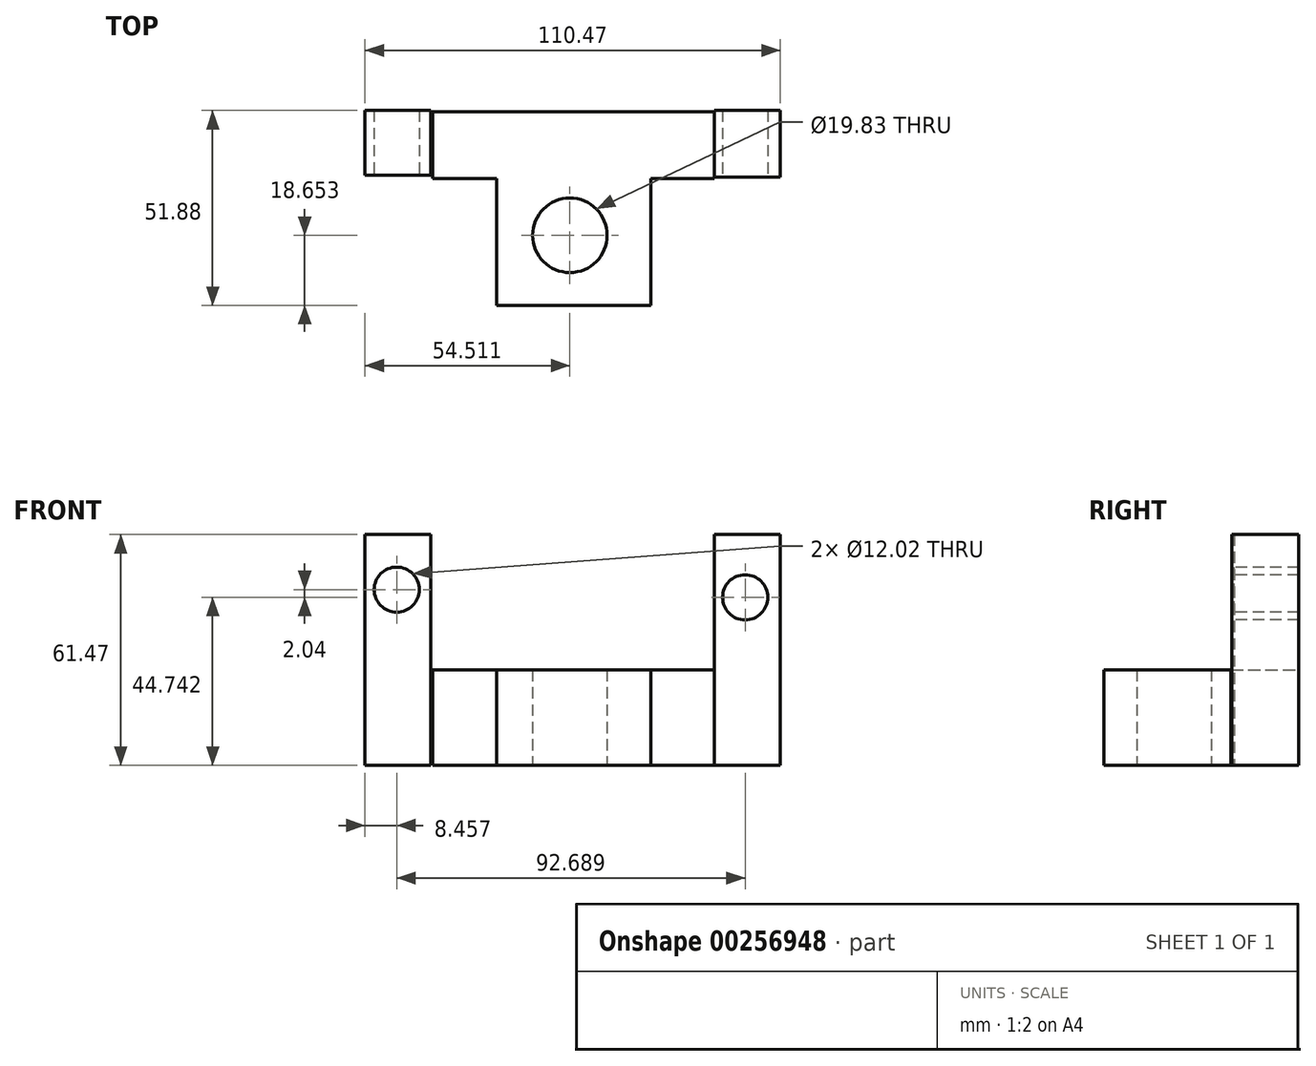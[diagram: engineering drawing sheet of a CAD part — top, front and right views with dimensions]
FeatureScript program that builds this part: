
annotation { "Feature Type Name" : "Feature", "Feature Type Description" : "" }
export const myFeature = defineFeature(function(context is Context, id is Id, definition is map)
    precondition{}
    {
        {
            var Q0;
            Q0=qCreatedBy(makeId("Top.planeOp"),FACE);
            var sketch = newSketch(context, id + "F0", { "sketchPlane" : qUnion([Q0])});
            skLineSegment(sketch, "E0", {"start": v(-25.36, 18.8) * mm, "end": v(-25.36, -15.01) * mm});
            skLineSegment(sketch, "E1", {"start": v(-25.36, -15.01) * mm, "end": v(15.74, -15.01) * mm});
            skLineSegment(sketch, "E2", {"start": v(15.74, -15.01) * mm, "end": v(15.74, 18.8) * mm});
            skLineSegment(sketch, "E3", {"start": v(15.74, 18.8) * mm, "end": v(32.65, 18.8) * mm});
            skLineSegment(sketch, "E4", {"start": v(32.65, 18.8) * mm, "end": v(32.65, 36.58) * mm});
            skLineSegment(sketch, "E5", {"start": v(-25.36, 18.8) * mm, "end": v(-42.26, 18.8) * mm});
            skLineSegment(sketch, "E6", {"start": v(-42.26, 18.8) * mm, "end": v(-42.26, 36.58) * mm});
            skLineSegment(sketch, "E7", {"start": v(-42.26, 36.58) * mm, "end": v(32.65, 36.58) * mm});
            skSolve(sketch);
        }
        {
            var Q0;
            Q0 = qSketchRegion(id + "F0", true);
            extrude(context, id + "F1", {"entities" : qUnion([Q0]), "depth" : 25.4 * mm});
        }
        {
            var Q0;
            Q0=qCreatedBy(makeId("Top.planeOp"),FACE);
            var sketch = newSketch(context, id + "F2", { "sketchPlane" : qUnion([Q0])});
            skLineSegment(sketch, "E8", {"start": v(32.65, 36.87) * mm, "end": v(32.65, 19.1) * mm});
            skLineSegment(sketch, "E9", {"start": v(32.65, 19.1) * mm, "end": v(50.13, 19.1) * mm});
            skLineSegment(sketch, "E10", {"start": v(50.13, 19.1) * mm, "end": v(50.13, 36.87) * mm});
            skLineSegment(sketch, "E11", {"start": v(50.13, 36.87) * mm, "end": v(32.65, 36.87) * mm});
            skLineSegment(sketch, "E12", {"start": v(-42.85, 36.87) * mm, "end": v(-60.34, 36.87) * mm});
            skLineSegment(sketch, "E13", {"start": v(-42.85, 36.87) * mm, "end": v(-42.85, 19.67) * mm});
            skLineSegment(sketch, "E14", {"start": v(-42.85, 19.67) * mm, "end": v(-60.34, 19.67) * mm});
            skLineSegment(sketch, "E15", {"start": v(-60.34, 19.67) * mm, "end": v(-60.34, 36.87) * mm});
            skSolve(sketch);
        }
        {
            var Q0;
            Q0 = qSketchRegion(id + "F2", true);
            extrude(context, id + "F3", {"entities" : qUnion([Q0]), "operationType" : NewBodyOperationType.ADD, "depth" : 61.47 * mm});
        }
        {
            var Q0;
            Q0=qCreatedBy(makeId("Top.planeOp"),FACE);
            var sketch = newSketch(context, id + "F4", { "sketchPlane" : qUnion([Q0])});
            skCircle(sketch, "E16", {"center": v(-5.83, 3.64) * mm, "radius": 9.91 * mm});
            skSolve(sketch);
        }
        {
            var Q0;
            Q0 = qSketchRegion(id + "F4", true);
            extrude(context, id + "F5", {"entities" : qUnion([Q0]), "operationType" : NewBodyOperationType.REMOVE, "depth" : 47.75 * mm});
        }
        {
            var Q0;
            Q0=qCreatedBy(makeId("Front.planeOp"),FACE);
            var sketch = newSketch(context, id + "F6", { "sketchPlane" : qUnion([Q0])});
            skCircle(sketch, "E17", {"center": v(26.73, 51.1) * mm, "radius": 4.65 * mm});
            skSolve(sketch);
        }
        {
            var Q0;
            Q0 = qSketchRegion(id + "F6", true);
            extrude(context, id + "F7", {"entities" : qUnion([Q0]), "operationType" : NewBodyOperationType.REMOVE, "oppositeDirection" : true, "depth" : 54.86 * mm});
        }
        {
            var Q0;
            Q0=makeQuery(id+"F3.opExtrude","SWEPT_FACE",FACE,{"disambiguationData":[OSD([sQuery(id+"F2.wireOp",EDGE,"E14")])]});
            var sketch = newSketch(context, id + "F8", { "sketchPlane" : qUnion([Q0])});
            skCircle(sketch, "E18", {"center": v(-51.88, 46.78) * mm, "radius": 6 * mm});
            skCircle(sketch, "E19", {"center": v(41.1, 44.45) * mm, "radius": 6 * mm});
            skSolve(sketch);
        }
        {
            var Q0;
            Q0=makeQuery(id+"F8.imprint","IMPRINT",FACE,{"disambiguationData":[TD([[makeQuery(id+"F8.imprint","IMPRINT",EDGE,{"derivedFrom":sQuery(id+"F8.wireOp",EDGE,"E18")}),1.0]])]});
            extrude(context, id + "F9", {"entities" : qUnion([Q0]), "operationType" : NewBodyOperationType.REMOVE, "oppositeDirection" : true, "depth" : 49.78 * mm});
        }
        {
            var Q0;
            Q0=qCreatedBy(makeId("Front.planeOp"),FACE);
            var sketch = newSketch(context, id + "F10", { "sketchPlane" : qUnion([Q0])});
            skCircle(sketch, "E20", {"center": v(40.8, 44.74) * mm, "radius": 6 * mm});
            skSolve(sketch);
        }
        {
            var Q0;
            Q0=makeQuery(id+"F10.imprint","IMPRINT",FACE,{"disambiguationData":[TD([[makeQuery(id+"F10.imprint","IMPRINT",EDGE,{"derivedFrom":sQuery(id+"F10.wireOp",EDGE,"E20")}),1.0]])]});
            var Q1;
            Q1=sQuery(id+"F10.wireOp",EDGE,"E20");
            extrude(context, id + "F11", {"entities" : qUnion([Q0]), "operationType" : NewBodyOperationType.REMOVE, "surfaceEntities" : qUnion([Q1]), "oppositeDirection" : true, "depth" : 51.05 * mm});
        }
    });
